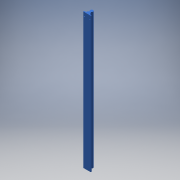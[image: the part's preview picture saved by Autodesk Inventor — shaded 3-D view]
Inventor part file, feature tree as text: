
AUTODESK INVENTOR PART (.ipt)
format: ipt  version: 2018 (Build 220112000, 112)  size: 141,824 bytes
history: native  units: mm
features: sketch x2, other x1, extrude x1, hole x1
ambient origin geometry x8: Origin, YZ Plane, XZ Plane, XY Plane, X Axis, Y Axis, Z Axis, Center Point
bodies: Body1 (feature_tree)
feature tree (5):
  other  "Sólido1"
  extrude  "Extrusão1"  Depth=25.0mm
  hole  "Furo1"  [1 undecoded]
  sketch  "Esboço1"  dims[d6=16.0mm d7=25.0mm]
  sketch  "Esboço3"  dims[d8=18.5mm d9=11.7mm d10=8.0mm d11=30.0deg d12=30.0deg d13=5.0mm d14=40.0mm d15=725.0mm d16=0.0mm d18=15.0mm d19=15.0mm d20=5.5mm d21=5.5mm d22=20.0mm d28=5.5mm d29=6.0mm d30=4.0mm d31=2.0mm d32=90.0deg d33=8.0mm d34=20.594885mm]
note: 1 required parameter value undecoded (feature->parameter linkage not recoverable at this tier; creation-order binding heuristic only, values carry confidence <= 0.55)
